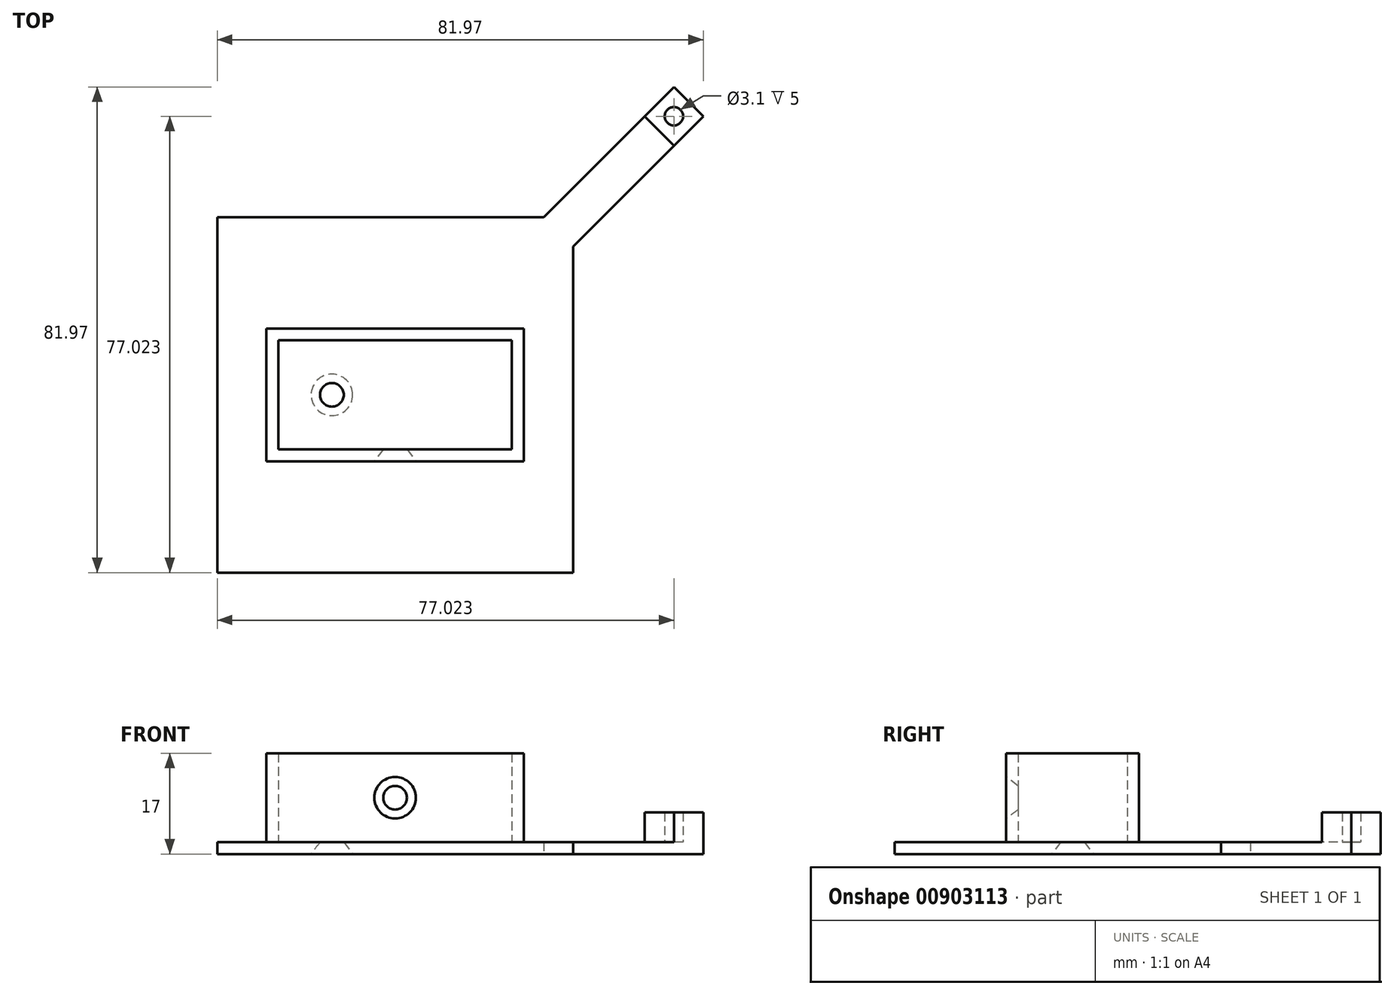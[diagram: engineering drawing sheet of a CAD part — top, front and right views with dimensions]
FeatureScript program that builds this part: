
annotation { "Feature Type Name" : "Feature", "Feature Type Description" : "" }
export const myFeature = defineFeature(function(context is Context, id is Id, definition is map)
    precondition{}
    {
        {
            var Q0;
            Q0=qCreatedBy(makeId("Top.planeOp"),FACE);
            var sketch = newSketch(context, id + "F0", { "sketchPlane" : qUnion([Q0])});
            skLineSegment(sketch, "E0.bottom", {"start": v(30, -30) * mm, "end": v(-30, -30) * mm});
            skLineSegment(sketch, "E0.top", {"start": v(30, 30) * mm, "end": v(-30, 30) * mm});
            skLineSegment(sketch, "E0.left", {"start": v(30, -30) * mm, "end": v(30, 30) * mm});
            skLineSegment(sketch, "E0.right", {"start": v(-30, -30) * mm, "end": v(-30, 30) * mm});
            skPoint(sketch, "E0.middle", {"position": v(0, 0) * mm});
            skLineSegment(sketch, "E1.bottom", {"start": v(19.5, -9) * mm, "end": v(-19.5, -9) * mm, "construction": true});
            skLineSegment(sketch, "E1.top", {"start": v(19.5, 9) * mm, "end": v(-19.5, 9) * mm, "construction": true});
            skLineSegment(sketch, "E1.left", {"start": v(19.5, -9) * mm, "end": v(19.5, 9) * mm, "construction": true});
            skLineSegment(sketch, "E1.right", {"start": v(-19.5, -9) * mm, "end": v(-19.5, 9) * mm, "construction": true});
            skLineSegment(sketch, "E2.0", {"start": v(19.7, 9.2) * mm, "end": v(-19.7, 9.2) * mm});
            skLineSegment(sketch, "E2.1", {"start": v(19.7, -9.2) * mm, "end": v(19.7, 9.2) * mm});
            skLineSegment(sketch, "E2.2", {"start": v(19.7, -9.2) * mm, "end": v(-19.7, -9.2) * mm});
            skLineSegment(sketch, "E2.3", {"start": v(-19.7, -9.2) * mm, "end": v(-19.7, 9.2) * mm});
            skLineSegment(sketch, "E3.0", {"start": v(21.7, 11.2) * mm, "end": v(-21.7, 11.2) * mm});
            skLineSegment(sketch, "E3.1", {"start": v(21.7, -11.2) * mm, "end": v(21.7, 11.2) * mm});
            skLineSegment(sketch, "E3.2", {"start": v(21.7, -11.2) * mm, "end": v(-21.7, -11.2) * mm});
            skLineSegment(sketch, "E3.3", {"start": v(-21.7, -11.2) * mm, "end": v(-21.7, 11.2) * mm});
            skCircle(sketch, "E4", {"center": v(-10.66, 0) * mm, "radius": 2 * mm});
            skLineSegment(sketch, "E5", {"start": v(0, 0) * mm, "end": v(0, 23.43) * mm, "construction": true});
            skPoint(sketch, "E5.endSnap0", {"position": v(0, 11.2) * mm});
            skSolve(sketch);
        }
        {
            var Q0;
            Q0=makeQuery(id+"F0.imprint","IMPRINT",FACE,{"disambiguationData":[TD([[makeQuery(id+"F0.imprint","IMPRINT",EDGE,{"derivedFrom":sQuery(id+"F0.wireOp",EDGE,"E0.bottom")}),-1.0]])]});
            var Q1;
            Q1=makeQuery(id+"F0.imprint","IMPRINT",FACE,{"disambiguationData":[TD([[makeQuery(id+"F0.imprint","IMPRINT",EDGE,{"derivedFrom":sQuery(id+"F0.wireOp",EDGE,"E2.0")}),-1.0]])]});
            var Q2;
            Q2=makeQuery(id+"F0.imprint","IMPRINT",FACE,{"disambiguationData":[TD([[makeQuery(id+"F0.imprint","IMPRINT",EDGE,{"derivedFrom":sQuery(id+"F0.wireOp",EDGE,"E2.0")}),1.0]])]});
            var Q3;
            Q3=makeQuery(id+"F0.imprint","IMPRINT",FACE,{"disambiguationData":[TD([[makeQuery(id+"F0.imprint","IMPRINT",EDGE,{"derivedFrom":sQuery(id+"F0.wireOp",EDGE,"E4")}),1.0]])]});
            var Q4;
            Q4=makeQuery(id+"F0.imprint","IMPRINT",FACE,{"disambiguationData":[TD([[makeQuery(id+"F0.imprint","IMPRINT",EDGE,{"derivedFrom":sQuery(id+"F0.wireOp",EDGE,"71976174-93c9-484e-bd24-1bdc720de17b0.MirrorC")}),-1.0]])]});
            extrude(context, id + "F1", {"entities" : qUnion([Q0, Q1, Q2, Q3, Q4]), "oppositeDirection" : true, "depth" : 2 * mm});
        }
        {
            var Q0;
            Q0=qCreatedBy(makeId("Top.planeOp"),FACE);
            var sketch = newSketch(context, id + "F2", { "sketchPlane" : qUnion([Q0])});
            skLineSegment(sketch, "E6", {"start": v(-2.47, 2.47) * mm, "end": v(2.47, -2.47) * mm});
            skLineSegment(sketch, "E7", {"start": v(2.47, -2.47) * mm, "end": v(51.97, 47.02) * mm});
            skLineSegment(sketch, "E8", {"start": v(51.97, 47.02) * mm, "end": v(47.02, 51.97) * mm});
            skLineSegment(sketch, "E9", {"start": v(-2.47, 2.47) * mm, "end": v(47.02, 51.97) * mm});
            skCircle(sketch, "E10", {"center": v(47.02, 47.02) * mm, "radius": 1.55 * mm});
            skLineSegment(sketch, "E11", {"start": v(42.07, 47.02) * mm, "end": v(47.02, 42.07) * mm});
            skLineSegment(sketch, "E12", {"start": v(47.02, 42.07) * mm, "end": v(51.97, 47.02) * mm});
            skLineSegment(sketch, "E13", {"start": v(49.5, 49.5) * mm, "end": v(44.55, 44.55) * mm, "construction": true});
            skPoint(sketch, "E14.0", {"position": v(30, 30) * mm});
            skLineSegment(sketch, "E15", {"start": v(30, 30) * mm, "end": v(0, 0) * mm, "construction": true});
            skSolve(sketch);
        }
        {
            var Q0;
            {var subQ1=sQuery(id+"F2.wireOp",EDGE,"E8");var subQ7=sQuery(id+"F2.wireOp",EDGE,"E6");Q0=qUnion([makeQuery(id+"F2.imprint","IMPRINT",FACE,{"disambiguationData":[TD([[makeQuery(id+"F2.imprint","IMPRINT",EDGE,{"derivedFrom":subQ7}),1.0]])]}),makeQuery(id+"F2.imprint","IMPRINT",FACE,{"disambiguationData":[TD([[makeQuery(id+"F2.imprint","IMPRINT",EDGE,{"derivedFrom":subQ1}),1.0]])]})]);}
            var Q1;
            Q1=makeQuery(id+"F2.imprint","IMPRINT",FACE,{"disambiguationData":[TD([[makeQuery(id+"F2.imprint","IMPRINT",EDGE,{"derivedFrom":sQuery(id+"F2.wireOp",EDGE,"E10")}),1.0]])]});
            extrude(context, id + "F3", {"entities" : qUnion([Q0, Q1]), "operationType" : NewBodyOperationType.ADD, "oppositeDirection" : true, "depth" : 2 * mm});
        }
        {
            var Q0;
            Q0=makeQuery(id+"F0.imprint","IMPRINT",FACE,{"disambiguationData":[TD([[makeQuery(id+"F0.imprint","IMPRINT",EDGE,{"derivedFrom":sQuery(id+"F0.wireOp",EDGE,"E2.0")}),-1.0]])]});
            extrude(context, id + "F4", {"entities" : qUnion([Q0]), "operationType" : NewBodyOperationType.ADD, "depth" : 15 * mm});
        }
        {
            var Q0;
            Q0=makeQuery(id+"F1.opExtrude","CAP_FACE",FACE,{"disambiguationData":[OSD([sQuery(id+"F0.wireOp",EDGE,"E0.bottom"),sQuery(id+"F0.wireOp",EDGE,"E0.top"),sQuery(id+"F0.wireOp",EDGE,"E0.left"),sQuery(id+"F0.wireOp",EDGE,"E0.right")])],"isStart":false});
            var sketch = newSketch(context, id + "F5", { "sketchPlane" : qUnion([Q0])});
            skPoint(sketch, "E16.1", {"position": v(-10.66, 0) * mm});
            skCircle(sketch, "E17", {"center": v(-10.66, 0) * mm, "radius": 3.5 * mm});
            skSolve(sketch);
        }
        {
            var Q1;
            Q1=makeQuery(id+"F0.imprint","IMPRINT",FACE,{"disambiguationData":[TD([[makeQuery(id+"F0.imprint","IMPRINT",EDGE,{"derivedFrom":sQuery(id+"F0.wireOp",EDGE,"E4")}),1.0]])]});
            var Q2;
            Q2=makeQuery(id+"F5.imprint","IMPRINT",FACE,{"disambiguationData":[TD([[makeQuery(id+"F5.imprint","IMPRINT",EDGE,{"derivedFrom":sQuery(id+"F5.wireOp",EDGE,"E17")}),1.0]])]});
            loft(context, id + "F6", {"operationType" : NewBodyOperationType.REMOVE, "sheetProfilesArray" : [{ "sheetProfileEntities" : qUnion([Q1]) }, { "sheetProfileEntities" : qUnion([Q2]) }]});
        }
        {
            var Q0;
            Q0=makeQuery(id+"F4.opExtrude","SWEPT_FACE",FACE,{"disambiguationData":[OSD([sQuery(id+"F0.wireOp",EDGE,"E3.2")])]});
            var sketch = newSketch(context, id + "F7", { "sketchPlane" : qUnion([Q0])});
            skPoint(sketch, "E18", {"position": v(0, 7.5) * mm});
            skPoint(sketch, "E18.positionSnap0", {"position": v(-21.7, 7.5) * mm});
            skCircle(sketch, "E19", {"center": v(0, 7.5) * mm, "radius": 3.5 * mm});
            skSolve(sketch);
        }
        {
            var Q0;
            Q0=makeQuery(id+"F4.opExtrude","SWEPT_FACE",FACE,{"disambiguationData":[OSD([sQuery(id+"F0.wireOp",EDGE,"E2.2")])]});
            var sketch = newSketch(context, id + "F8", { "sketchPlane" : qUnion([Q0])});
            skPoint(sketch, "E20.0", {"position": v(0, 7.5) * mm});
            skCircle(sketch, "E21", {"center": v(0, 7.5) * mm, "radius": 2 * mm});
            skSolve(sketch);
        }
        {
            var Q1;
            Q1=makeQuery(id+"F7.imprint","IMPRINT",FACE,{"disambiguationData":[TD([[makeQuery(id+"F7.imprint","IMPRINT",EDGE,{"derivedFrom":sQuery(id+"F7.wireOp",EDGE,"E19")}),1.0]])]});
            var Q2;
            Q2=makeQuery(id+"F8.imprint","IMPRINT",FACE,{"disambiguationData":[TD([[makeQuery(id+"F8.imprint","IMPRINT",EDGE,{"derivedFrom":sQuery(id+"F8.wireOp",EDGE,"E21")}),1.0]])]});
            loft(context, id + "F9", {"operationType" : NewBodyOperationType.REMOVE, "sheetProfilesArray" : [{ "sheetProfileEntities" : qUnion([Q1]) }, { "sheetProfileEntities" : qUnion([Q2]) }]});
        }
        {
            var Q0;
            {var subQ1=sQuery(id+"F2.wireOp",EDGE,"E8");Q0=makeQuery(id+"F2.imprint","IMPRINT",FACE,{"disambiguationData":[TD([[makeQuery(id+"F2.imprint","IMPRINT",EDGE,{"derivedFrom":subQ1}),1.0]])]});}
            extrude(context, id + "F10", {"entities" : qUnion([Q0]), "operationType" : NewBodyOperationType.ADD, "depth" : 5 * mm});
        }
    });
